# Revit family: Haworth_BuzziHat_Light
name_source: partatom
category: Lighting Fixtures
revit_build: Autodesk Revit 2018 (Build: 20170223_1515(x64)
units: mm (PartAtom-declared; Revit-internal decimal feet)

## family parameters
Cut with Voids When Loaded = No
Host = Face
Light Source = No
Part Type = Normal
Room Calculation Point = No
Round Connector Dimension = Use Diameter
Shared = No

## types (4) — shared parameters
Actual Depth = 20.47 "
Actual Width = 20.47 "
Assembly Code = E2020200
Glass Finish = Haworth _ Glass _ Frosted
Manufacturer = Haworth
Max. Cable Length = 196.85 "
Min. Cable Length = 10 "
Model = HCBZ-HTP
Note = Verify Final Dim. w/ Haworth
Revision = 1
URL = http://www.haworth.com
URL - Product = https://www.haworth.com
Warranty = http://www.haworth.com
zero-valued in all types: Default Elevation

## per-type parameters (varying)
| type | Actual Height | Description | Extra Large | Large | Medium | Small |
| HCBZ-HTP3 - Large | 20.47 " | Haworth BuzziHat Pendant Light Large | No | Yes | No | No |
| HCBZ-HTP2 - Medium | 16.54 " | Haworth BuzziHat Pendant Light Medium | No | No | Yes | No |
| HCBZ-HTP1 - Small | 11.02 " | Haworth BuzziHat Pendant Light Small | No | No | No | Yes |
| HCBZ-HTP4 - Extra Large | 24.41 " | Haworth BuzziHat Pendant Light Extra Large | Yes | No | No | No |

## geometry (parser evidence)
native form markers: Sweep x5
no freeform markers — native parametric forms only
